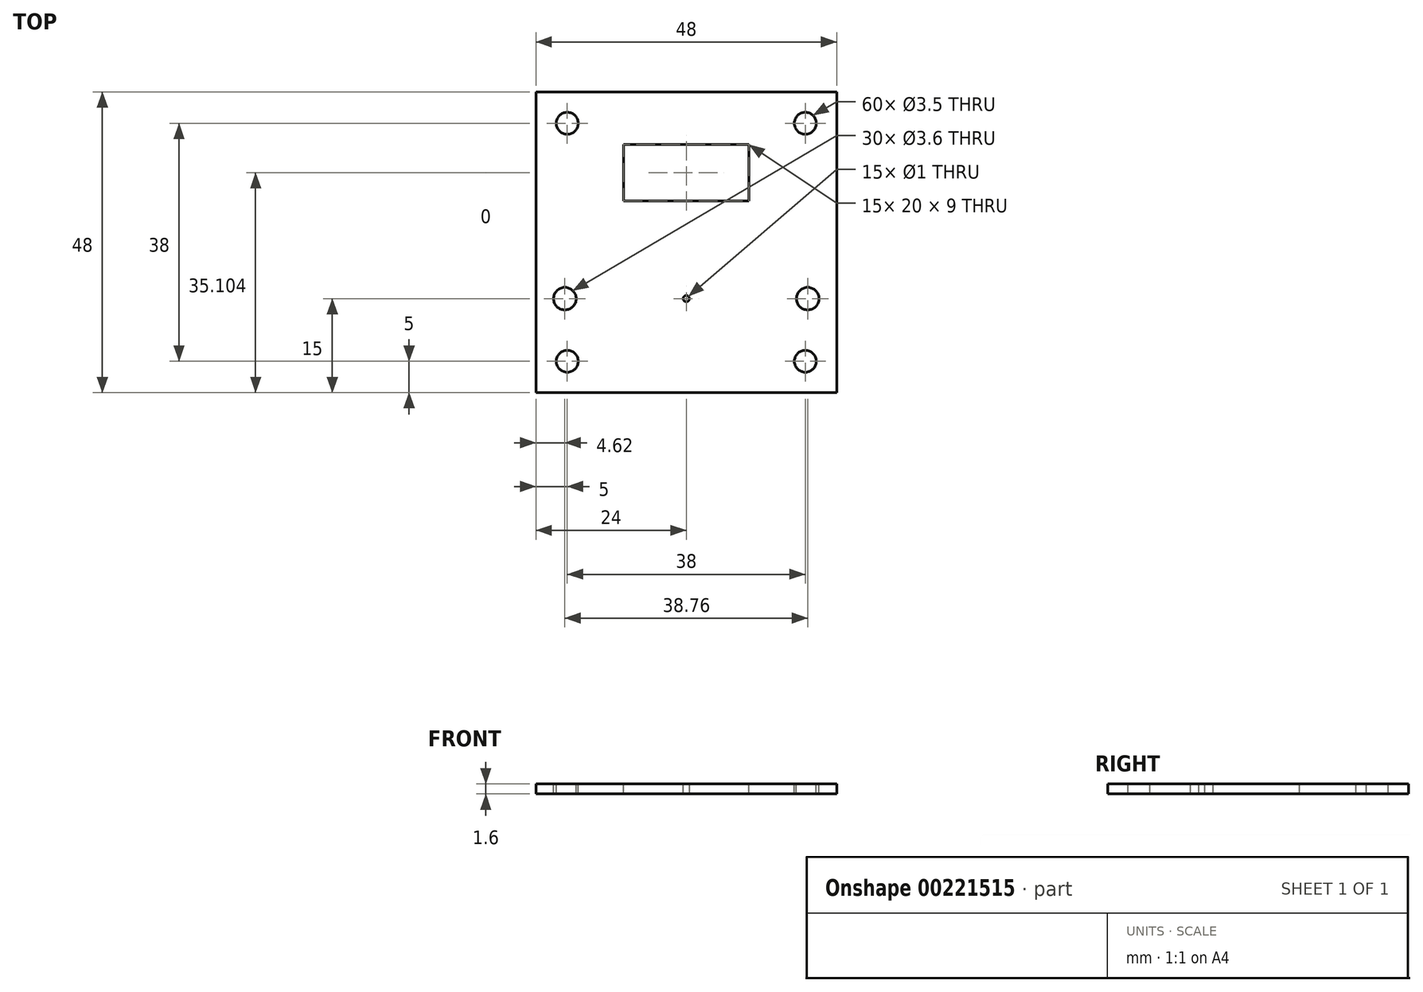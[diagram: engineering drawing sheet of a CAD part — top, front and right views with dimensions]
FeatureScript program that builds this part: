
annotation { "Feature Type Name" : "Feature", "Feature Type Description" : "" }
export const myFeature = defineFeature(function(context is Context, id is Id, definition is map)
    precondition{}
    {
        {
            var Q0;
            Q0=qCreatedBy(makeId("Right.planeOp"),FACE);
            var sketch = newSketch(context, id + "F0", { "sketchPlane" : qUnion([Q0])});
            skLineSegment(sketch, "E0.bottom", {"start": v(24, -0.8) * mm, "end": v(-24, -0.8) * mm});
            skLineSegment(sketch, "E0.top", {"start": v(24, 0.8) * mm, "end": v(-24, 0.8) * mm});
            skLineSegment(sketch, "E0.left", {"start": v(24, -0.8) * mm, "end": v(24, 0.8) * mm});
            skLineSegment(sketch, "E0.right", {"start": v(-24, -0.8) * mm, "end": v(-24, 0.8) * mm});
            skPoint(sketch, "E0.middle", {"position": v(0, 0) * mm});
            skSolve(sketch);
        }
        {
            var Q0;
            Q0=makeQuery(id+"F0.imprint","IMPRINT",FACE,{"disambiguationData":[TD([[makeQuery(id+"F0.imprint","IMPRINT",EDGE,{"derivedFrom":sQuery(id+"F0.wireOp",EDGE,"E0.bottom")}),-1.0]])]});
            extrude(context, id + "F1", {"entities" : qUnion([Q0]), "oppositeDirection" : true, "depth" : 48 * mm});
        }
        {
            var Q0;
            Q0=makeQuery(id+"F1.opExtrude","SWEPT_FACE",FACE,{"disambiguationData":[OSD([sQuery(id+"F0.wireOp",EDGE,"E0.top")])]});
            var sketch = newSketch(context, id + "F2", { "sketchPlane" : qUnion([Q0])});
            skLineSegment(sketch, "E1", {"start": v(-43, -24) * mm, "end": v(-43, 24) * mm, "construction": true});
            skLineSegment(sketch, "E2", {"start": v(-48, -19) * mm, "end": v(0, -19) * mm, "construction": true});
            skPoint(sketch, "E3", {"position": v(-43, -19) * mm});
            skCircle(sketch, "E4", {"center": v(-43, -19) * mm, "radius": 1.75 * mm});
            skLineSegment(sketch, "E5", {"start": v(-48, 19) * mm, "end": v(0, 19) * mm, "construction": true});
            skPoint(sketch, "E6", {"position": v(-43, 19) * mm});
            skCircle(sketch, "E7", {"center": v(-43, 19) * mm, "radius": 1.75 * mm});
            skLineSegment(sketch, "E8", {"start": v(-24, 24) * mm, "end": v(-24, -24) * mm, "construction": true});
            skLineSegment(sketch, "E9", {"start": v(-48, -9) * mm, "end": v(0, -9) * mm, "construction": true});
            skLineSegment(sketch, "E10", {"start": v(-43.38, -6.99) * mm, "end": v(-43.38, -11.87) * mm, "construction": true});
            skLineSegment(sketch, "E11", {"start": v(-4.62, -6.64) * mm, "end": v(-4.62, -12.54) * mm, "construction": true});
            skPoint(sketch, "E12", {"position": v(-24, -9) * mm});
            skCircle(sketch, "E13", {"center": v(-43.38, -9) * mm, "radius": 1.8 * mm});
            skPoint(sketch, "E14", {"position": v(-4.62, -9) * mm});
            skCircle(sketch, "E15", {"center": v(-4.62, -9) * mm, "radius": 1.8 * mm});
            skLineSegment(sketch, "E16", {"start": v(-5, 24) * mm, "end": v(-5, -24) * mm, "construction": true});
            skPoint(sketch, "E17", {"position": v(-5, 19) * mm});
            skPoint(sketch, "E18", {"position": v(-5, -19) * mm});
            skCircle(sketch, "E19", {"center": v(-5, 19) * mm, "radius": 1.75 * mm});
            skCircle(sketch, "E20", {"center": v(-5, -19) * mm, "radius": 1.75 * mm});
            skCircle(sketch, "E21", {"center": v(-24, -9) * mm, "radius": 0.5 * mm});
            skLineSegment(sketch, "E22", {"start": v(-37.3, 24) * mm, "end": v(-37.3, -24) * mm, "construction": true});
            skLineSegment(sketch, "E23", {"start": v(-48, 6.6) * mm, "end": v(0, 6.6) * mm, "construction": true});
            skLineSegment(sketch, "E24", {"start": v(-48, 11.1) * mm, "end": v(0, 11.1) * mm, "construction": true});
            skPoint(sketch, "E25", {"position": v(-24, 11.1) * mm});
            skSolve(sketch);
        }
        {
            var Q0;
            Q0 = qSketchRegion(id + "F2", true);
            extrude(context, id + "F3", {"entities" : qUnion([Q0]), "operationType" : NewBodyOperationType.REMOVE, "endBound" : BoundingType.THROUGH_ALL, "oppositeDirection" : true, "depth" : 25 * mm});
        }
        {
            var Q0;
            Q0=makeQuery(id+"F1.opExtrude","SWEPT_FACE",FACE,{"disambiguationData":[OSD([sQuery(id+"F0.wireOp",EDGE,"E0.top")])]});
            var sketch = newSketch(context, id + "F4", { "sketchPlane" : qUnion([Q0])});
            skLineSegment(sketch, "E26", {"start": v(-40.84, 6.6) * mm, "end": v(-9.45, 6.6) * mm, "construction": true});
            skLineSegment(sketch, "E27", {"start": v(-24, 24) * mm, "end": v(-24, 6.6) * mm, "construction": true});
            skLineSegment(sketch, "E28", {"start": v(-27.67, 11.1) * mm, "end": v(-14, 11.1) * mm, "construction": true});
            skPoint(sketch, "E29", {"position": v(-24, 11.1) * mm});
            skLineSegment(sketch, "E30.bottom", {"start": v(-14, 6.6) * mm, "end": v(-34, 6.6) * mm});
            skLineSegment(sketch, "E30.top", {"start": v(-14, 15.6) * mm, "end": v(-34, 15.6) * mm});
            skLineSegment(sketch, "E30.left", {"start": v(-14, 6.6) * mm, "end": v(-14, 15.6) * mm});
            skLineSegment(sketch, "E30.right", {"start": v(-34, 6.6) * mm, "end": v(-34, 15.6) * mm});
            skSolve(sketch);
        }
        {
            var Q0;
            Q0=makeQuery(id+"F4.imprint","IMPRINT",FACE,{"disambiguationData":[TD([[makeQuery(id+"F4.imprint","IMPRINT",EDGE,{"derivedFrom":sQuery(id+"F4.wireOp",EDGE,"E30.bottom")}),-1.0]])]});
            extrude(context, id + "F5", {"entities" : qUnion([Q0]), "operationType" : NewBodyOperationType.REMOVE, "endBound" : BoundingType.THROUGH_ALL, "oppositeDirection" : true, "depth" : 25 * mm});
        }
        {
            var Q0;
            Q0=qCreatedBy(makeId("Top.planeOp"),FACE);
            var sketch = newSketch(context, id + "F6", { "sketchPlane" : qUnion([Q0])});
            skLineSegment(sketch, "E31.bottom", {"start": v(24, 24) * mm, "end": v(-24, 24) * mm});
            skLineSegment(sketch, "E31.top", {"start": v(24, -24) * mm, "end": v(-24, -24) * mm});
            skLineSegment(sketch, "E31.left", {"start": v(24, 24) * mm, "end": v(24, -24) * mm});
            skLineSegment(sketch, "E31.right", {"start": v(-24, 24) * mm, "end": v(-24, -24) * mm});
            skPoint(sketch, "E31.middle", {"position": v(0, 0) * mm});
            skCircle(sketch, "E32", {"center": v(-19, 19) * mm, "radius": 1.75 * mm});
            skCircle(sketch, "E33", {"center": v(19, 19) * mm, "radius": 1.75 * mm});
            skCircle(sketch, "E34", {"center": v(-19, -19) * mm, "radius": 1.75 * mm});
            skCircle(sketch, "E35", {"center": v(19, -19) * mm, "radius": 1.75 * mm});
            skLineSegment(sketch, "E36.bottom", {"start": v(10, 19) * mm, "end": v(-10, 19) * mm});
            skLineSegment(sketch, "E36.top", {"start": v(10, 10) * mm, "end": v(-10, 10) * mm});
            skLineSegment(sketch, "E36.left", {"start": v(10, 19) * mm, "end": v(10, 10) * mm});
            skLineSegment(sketch, "E36.right", {"start": v(-10, 19) * mm, "end": v(-10, 10) * mm});
            skPoint(sketch, "E36.middle", {"position": v(0, 14.5) * mm});
            skSolve(sketch);
        }
        {
            var Q0;
            Q0 = qSketchRegion(id + "F6", true);
            extrude(context, id + "F7", {"entities" : qUnion([Q0]), "depth" : 5 * mm});
        }
        {
            var Q0;
            Q0=makeQuery(id+"F7.opExtrude","SWEPT_BODY",BODY,{"disambiguationData":[OSD([sQuery(id+"F6.wireOp",EDGE,"E31.bottom"),sQuery(id+"F6.wireOp",EDGE,"E31.top"),sQuery(id+"F6.wireOp",EDGE,"E31.left"),sQuery(id+"F6.wireOp",EDGE,"E31.right"),sQuery(id+"F6.wireOp",EDGE,"E32"),sQuery(id+"F6.wireOp",EDGE,"E33"),sQuery(id+"F6.wireOp",EDGE,"E34"),sQuery(id+"F6.wireOp",EDGE,"E35"),sQuery(id+"F6.wireOp",EDGE,"E36.bottom"),sQuery(id+"F6.wireOp",EDGE,"E36.top"),sQuery(id+"F6.wireOp",EDGE,"E36.left"),sQuery(id+"F6.wireOp",EDGE,"E36.right")])]});
            deleteBodies(context, id + "F8", {"entities" : qUnion([Q0])});
        }
    });
